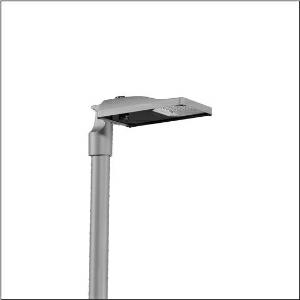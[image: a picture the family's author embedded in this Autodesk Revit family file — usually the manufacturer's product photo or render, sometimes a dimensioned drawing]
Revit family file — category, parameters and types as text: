
# Revit family: streetlight_sl_31_micro___st0_5a_5xh5b31t08da_db8b
name_source: partatom
category: Lighting Fixtures
units: mm (PartAtom-declared; Revit-internal decimal feet)

## family parameters
Cut with Voids When Loaded = No
Host = Face
Light Source = No
Part Type = Normal
Room Calculation Point = No
Round Connector Dimension = Use Diameter
Shared = No

## types (1)
- --- (1 x LED, 4940 lm, 37.7 W, 3000K)
    Apparent Load = 38 VA
    CIE Flux Codes = 41 75 97 100 100
    Color Rendering = 70
    Color Temperature = 3000K
    Default Elevation = 1800 mm
    Description = Streetlight SL 31 micro D4i, Desk-Remote mast luminaire for post-top, side-entry; light control with lens of PMMA; light distribution: ST0.5a, direct asymmetric distribution, for standard-compliant lighting for roads and squares; LED: luminous flux: 4.940lm, light colour: 730, colour temperature: 3000K; luminous efficacy: 131lm/W; control: pre-setting: logarithmic dimming characteristic, flexible luminous flux parameterisation, time-dependent luminous flux control, constant luminous flux control, power reduction, intelligent temperature release in ECG and LED module, overheat protection; luminaire housing, of diecast aluminium, SITECO metallic grey (DB 702S), corrosivity category C5 high according to DIN EN ISO 12944; cover of toughened safety glass, transparent, opened without tools; mast flange of diecast aluminium, SITECO metallic grey (DB 702S), spigot size: 76/60mm, mast flange included unmounted; with cable H07RN-F 2x 1.5mm², cable length: 6,5m, connection cable pre-assembled; mains connection: 220..240V, AC, 50/60Hz; power consumption (at start of service life): 37,7W / (at end of service life): 40,9W / (with reduced operation 50%): 16,3W; protection rating (complete): IP66; insulation class (complete): insulation class II (safety insulation); impact resistance: IK09; certification: CE, ENEC, ENEC+, VDE, UKCA, ZD4i; permissible operating ambient temperature for outdoor applications: -40..+50°C; packaging unit: 1 piece

Light Distribution: ST0.5a
    Height = 76 mm
    Lamp = 1 x LED
    Lamp Light Flux = 4940 lm
    Lamp Power = 37.7 W
    Lamp count = 1
    Length = 467 mm
    Luminous efficacy = 131 lm/W
    Manufacturer = Siteco
    ModVariant = No
    Model = 5XH5B31T08DA
    Number of Poles = 1
    OnlyDefault = Yes
    Power Factor = 1
    Product Name = Streetlight SL 31 micro | ST0.5a
    Product group = mast luminaire | pylon top
    ProductGroupID = 6100
    Protection Class = Protection class II
    Protection Degree = IP 66
    RLX_Detail_Level = 1
    RLX_Emergency_Light_Flux = 0 lm
    RLX_Emergency_Type = 0
    RLX_Emergency_Type_DB = No
    RlxData = <blob elided: 55117 chars, md5=12a3f6a3>
    Socket = socket
    Standby Power = 0 W
    System Light Flux = 4940 lm
    System Power = 38 W
    Type Comments = factory setting: luminous flux: 100 % | dim-lin: 254 | 745 mA
    Type Image = l_1300315.jpg
    URL = http://relux.com
    VarID = @adj_055581
    Voltage = 0 V
    Weight = 0.00 kg
    Width = 265 mm

## geometry (parser evidence)
native form markers: Blend x4, Sweep x11
no freeform markers — native parametric forms only
